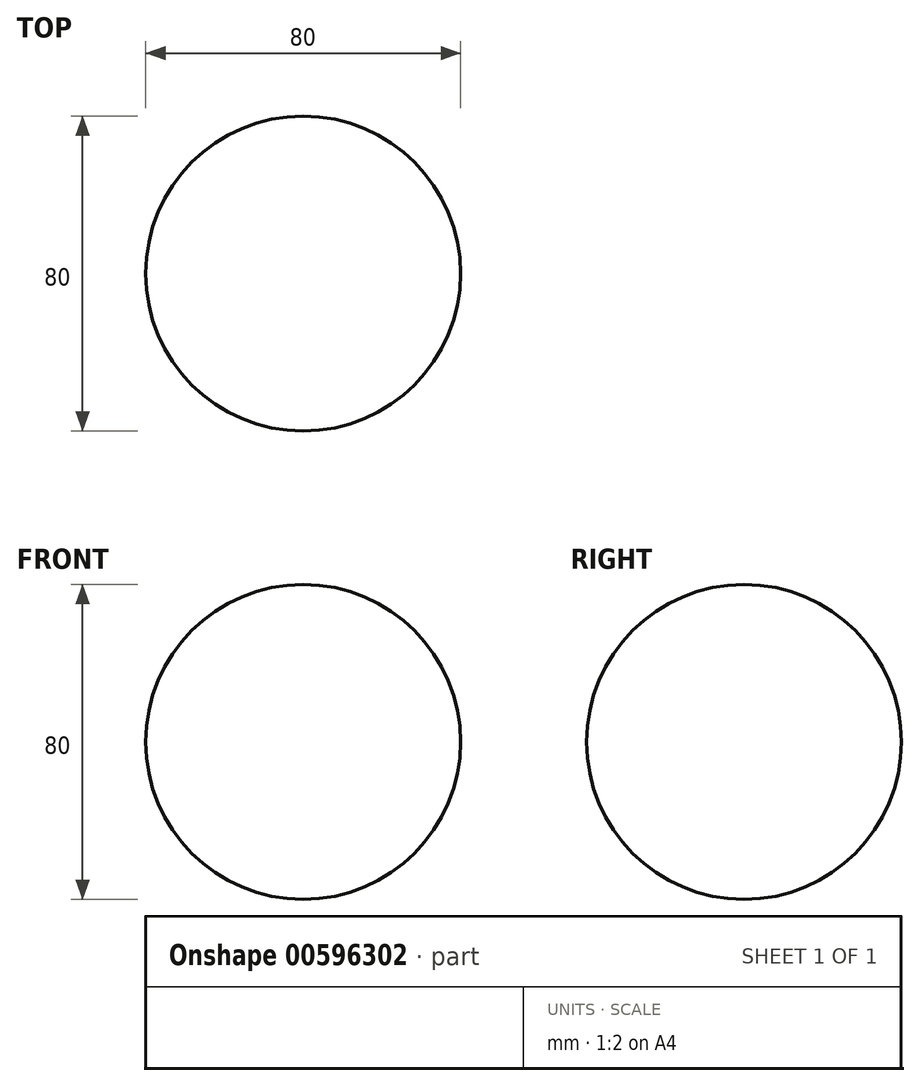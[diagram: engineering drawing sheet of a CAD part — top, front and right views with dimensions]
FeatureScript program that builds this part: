
annotation { "Feature Type Name" : "Feature", "Feature Type Description" : "" }
export const myFeature = defineFeature(function(context is Context, id is Id, definition is map)
    precondition{}
    {
        {
            var Q0;
            Q0=qCreatedBy(makeId("Top.planeOp"),FACE);
            var sketch = newSketch(context, id + "F0", { "sketchPlane" : qUnion([Q0])});
            skArc(sketch, "E0", {"start": v(0, -40) * mm, "mid": v(40, 0) * mm, "end": v(0, 40) * mm});
            skLineSegment(sketch, "E1", {"start": v(0, 40) * mm, "end": v(0, -40) * mm});
            skSolve(sketch);
        }
        {
            var Q0;
            Q0 = qSketchRegion(id + "F0", true);
            var Q1;
            Q1 = qConstructionFilter(qBodyType(qCreatedBy(id + "F0" ,EDGE), BodyType.WIRE), ConstructionObject.NO);
            var Q2;
            Q2=sQuery(id+"F0.wireOp",EDGE,"E1");
            revolve(context, id + "F1", {"entities" : qUnion([Q0]), "surfaceEntities" : qUnion([Q1]), "axis" : qUnion([Q2]), "revolveType" : RevolveType.FULL});
        }
    });
